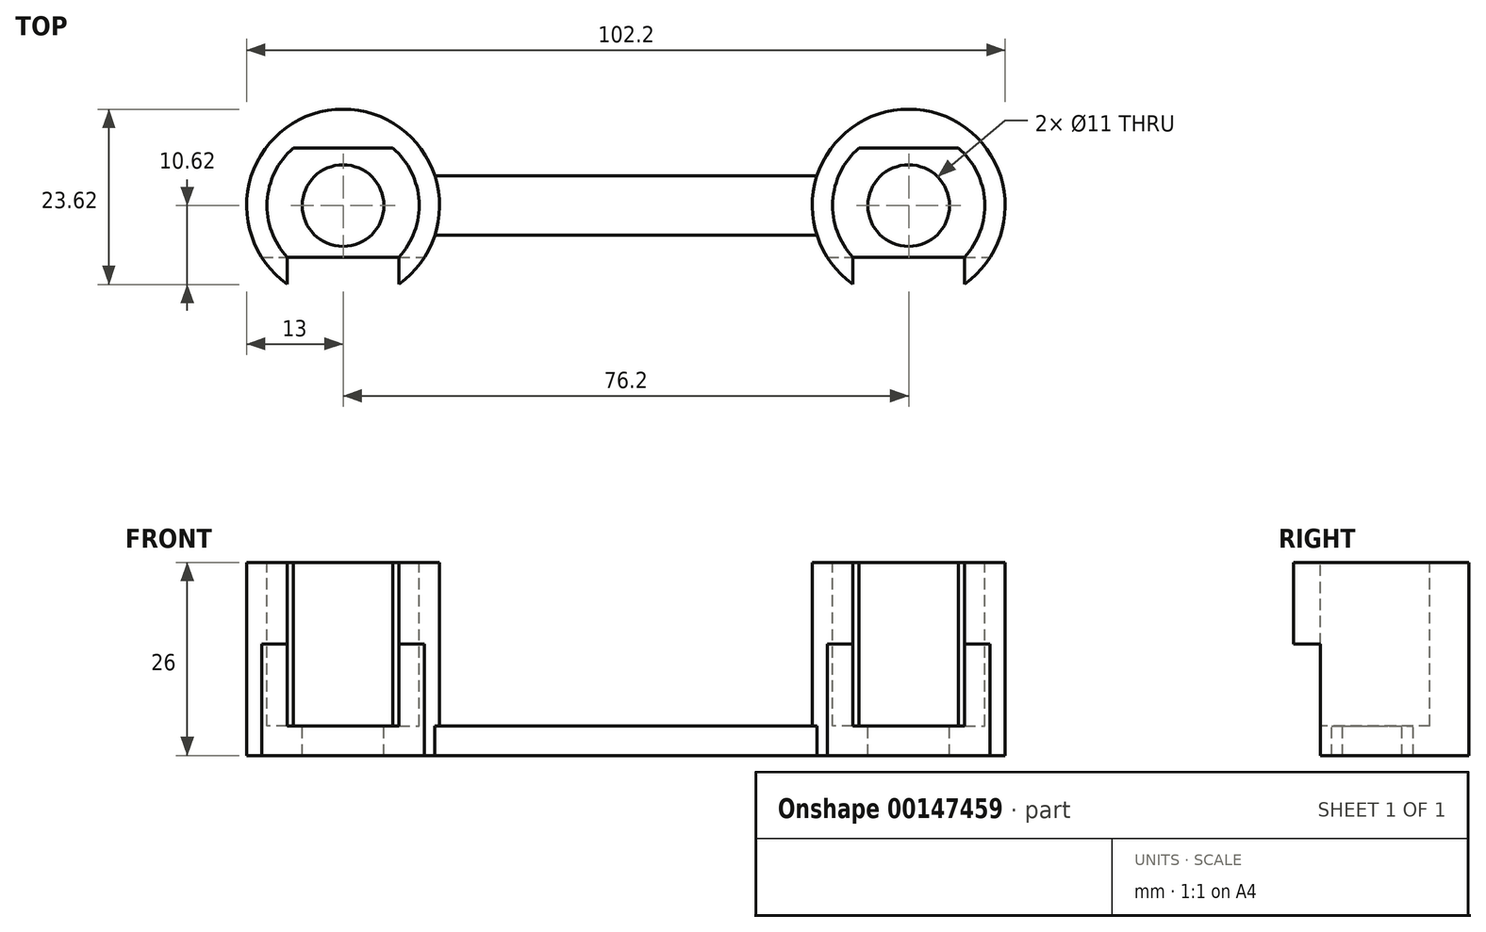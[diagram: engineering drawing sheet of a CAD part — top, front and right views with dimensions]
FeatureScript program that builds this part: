
annotation { "Feature Type Name" : "Feature", "Feature Type Description" : "" }
export const myFeature = defineFeature(function(context is Context, id is Id, definition is map)
    precondition{}
    {
        {
            var Q0;
            Q0=qCreatedBy(makeId("Top.planeOp"),FACE);
            var sketch = newSketch(context, id + "F0", { "sketchPlane" : qUnion([Q0])});
            skPoint(sketch, "E0.middle", {"position": v(-38.1, 0) * mm});
            skPoint(sketch, "E1.orphan", {"position": v(-46.9, 8.41) * mm});
            skPoint(sketch, "E0.left.end.orphan", {"position": v(-49.35, -8.41) * mm});
            skPoint(sketch, "E2.orphan", {"position": v(-29.3, -8.41) * mm});
            skPoint(sketch, "E3.orphan", {"position": v(-26.85, 8.41) * mm});
            skCircle(sketch, "E4", {"center": v(-38.1, 0) * mm, "radius": 13 * mm});
            skPoint(sketch, "E5.middle", {"position": v(38.1, 0) * mm});
            skPoint(sketch, "E6.orphan", {"position": v(29.32, 8.41) * mm});
            skPoint(sketch, "E5.left.end.orphan", {"position": v(26.83, -8.41) * mm});
            skPoint(sketch, "E7.orphan", {"position": v(46.88, -8.41) * mm});
            skPoint(sketch, "E8.orphan", {"position": v(49.37, 8.41) * mm});
            skCircle(sketch, "E9", {"center": v(38.1, 0) * mm, "radius": 13 * mm});
            skLineSegment(sketch, "E10", {"start": v(-38.1, 0) * mm, "end": v(38.1, 0) * mm});
            skSolve(sketch);
        }
        {
            var Q0;
            Q0=qCreatedBy(makeId("Top.planeOp"),FACE);
            var sketch = newSketch(context, id + "F1", { "sketchPlane" : qUnion([Q0])});
            skLineSegment(sketch, "E11", {"start": v(38.1, 0) * mm, "end": v(-38.1, 0) * mm});
            skCircle(sketch, "E12", {"center": v(-38.1, 0) * mm, "radius": 10.25 * mm});
            skCircle(sketch, "E13", {"center": v(38.1, 0) * mm, "radius": 10.25 * mm});
            skLineSegment(sketch, "E14.bottom", {"start": v(-44.8, 7.76) * mm, "end": v(-31.4, 7.76) * mm});
            skLineSegment(sketch, "E14.top", {"start": v(-44.8, -7.76) * mm, "end": v(-31.4, -7.76) * mm});
            skLineSegment(sketch, "E14.left", {"start": v(-44.8, 7.76) * mm, "end": v(-44.8, -7.76) * mm});
            skLineSegment(sketch, "E14.right", {"start": v(-31.4, 7.76) * mm, "end": v(-31.4, -7.76) * mm});
            skLineSegment(sketch, "E15.bottom", {"start": v(44.8, 7.76) * mm, "end": v(31.4, 7.76) * mm});
            skLineSegment(sketch, "E15.top", {"start": v(44.8, -7.76) * mm, "end": v(31.4, -7.76) * mm});
            skLineSegment(sketch, "E15.left", {"start": v(44.8, 7.76) * mm, "end": v(44.8, -7.76) * mm});
            skLineSegment(sketch, "E15.right", {"start": v(31.4, 7.76) * mm, "end": v(31.4, -7.76) * mm});
            skSolve(sketch);
        }
        {
            var Q0;
            Q0 = qSketchRegion(id + "F0", true);
            extrude(context, id + "F2", {"entities" : qUnion([Q0]), "oppositeDirection" : true, "depth" : 26 * mm});
        }
        {
            var Q0;
            {var subQ0=sQuery(id+"F1.wireOp",EDGE,"E12");var subQ1=sQuery(id+"F1.wireOp",EDGE,"E11");var subQ2=makeQuery(id+"F1.imprint","INTERSECT",VERTEX,{"derivedFrom":[subQ1,subQ0]});Q0=makeQuery(id+"F1.imprint","IMPRINT",FACE,{"disambiguationData":[TD([[makeQuery(id+"F1.imprint","IMPRINT",EDGE,{"disambiguationData":[TD([[subQ2,-1.0]])],"derivedFrom":subQ1}),1.0]])]});}
            var Q1;
            {var subQ0=sQuery(id+"F1.wireOp",EDGE,"E12");var subQ1=sQuery(id+"F1.wireOp",EDGE,"E11");var subQ2=makeQuery(id+"F1.imprint","INTERSECT",VERTEX,{"derivedFrom":[subQ1,subQ0]});Q1=makeQuery(id+"F1.imprint","IMPRINT",FACE,{"disambiguationData":[TD([[makeQuery(id+"F1.imprint","IMPRINT",EDGE,{"disambiguationData":[TD([[subQ2,-1.0]])],"derivedFrom":subQ1}),-1.0]])]});}
            var Q2;
            {var subQ1=sQuery(id+"F1.wireOp",EDGE,"E14.bottom");Q2=makeQuery(id+"F1.imprint","IMPRINT",FACE,{"disambiguationData":[TD([[makeQuery(id+"F1.imprint","IMPRINT",EDGE,{"derivedFrom":subQ1}),-1.0]])]});}
            var Q3;
            {var subQ0=sQuery(id+"F1.wireOp",EDGE,"E14.left");Q3=makeQuery(id+"F1.imprint","IMPRINT",FACE,{"disambiguationData":[TD([[makeQuery(id+"F1.imprint","IMPRINT",EDGE,{"derivedFrom":subQ0}),-1.0]])]});}
            var Q4;
            {var subQ1=sQuery(id+"F1.wireOp",EDGE,"E15.bottom");Q4=makeQuery(id+"F1.imprint","IMPRINT",FACE,{"disambiguationData":[TD([[makeQuery(id+"F1.imprint","IMPRINT",EDGE,{"derivedFrom":subQ1}),1.0]])]});}
            var Q5;
            {var subQ0=sQuery(id+"F1.wireOp",EDGE,"E15.left");Q5=makeQuery(id+"F1.imprint","IMPRINT",FACE,{"disambiguationData":[TD([[makeQuery(id+"F1.imprint","IMPRINT",EDGE,{"derivedFrom":subQ0}),1.0]])]});}
            var Q6;
            {var subQ0=sQuery(id+"F1.wireOp",EDGE,"E13");var subQ1=sQuery(id+"F1.wireOp",EDGE,"E11");var subQ2=makeQuery(id+"F1.imprint","INTERSECT",VERTEX,{"derivedFrom":[subQ1,subQ0]});Q6=makeQuery(id+"F1.imprint","IMPRINT",FACE,{"disambiguationData":[TD([[makeQuery(id+"F1.imprint","IMPRINT",EDGE,{"disambiguationData":[TD([[subQ2,1.0]])],"derivedFrom":subQ1}),1.0]])]});}
            var Q7;
            {var subQ0=sQuery(id+"F1.wireOp",EDGE,"E13");var subQ1=sQuery(id+"F1.wireOp",EDGE,"E11");var subQ2=makeQuery(id+"F1.imprint","INTERSECT",VERTEX,{"derivedFrom":[subQ1,subQ0]});Q7=makeQuery(id+"F1.imprint","IMPRINT",FACE,{"disambiguationData":[TD([[makeQuery(id+"F1.imprint","IMPRINT",EDGE,{"disambiguationData":[TD([[subQ2,1.0]])],"derivedFrom":subQ1}),-1.0]])]});}
            extrude(context, id + "F3", {"entities" : qUnion([Q0, Q1, Q2, Q3, Q4, Q5, Q6, Q7]), "operationType" : NewBodyOperationType.REMOVE, "oppositeDirection" : true, "depth" : 22 * mm});
        }
        {
            var Q0;
            Q0=qCreatedBy(makeId("Top.planeOp"),FACE);
            var sketch = newSketch(context, id + "F4", { "sketchPlane" : qUnion([Q0])});
            skLineSegment(sketch, "E16", {"start": v(38.1, 0) * mm, "end": v(-38.1, 0) * mm});
            skCircle(sketch, "E17", {"center": v(-38.1, 0) * mm, "radius": 5.5 * mm});
            skCircle(sketch, "E18", {"center": v(38.1, 0) * mm, "radius": 5.5 * mm});
            skLineSegment(sketch, "E19", {"start": v(-38.1, 0) * mm, "end": v(-38.1, -10) * mm});
            skLineSegment(sketch, "E20.bottom", {"start": v(-45.6, -13) * mm, "end": v(-30.6, -13) * mm});
            skLineSegment(sketch, "E20.top", {"start": v(-45.6, -6.99) * mm, "end": v(-30.6, -6.99) * mm});
            skLineSegment(sketch, "E20.left", {"start": v(-45.6, -13) * mm, "end": v(-45.6, -6.99) * mm});
            skLineSegment(sketch, "E20.right", {"start": v(-30.6, -13) * mm, "end": v(-30.6, -6.99) * mm});
            skPoint(sketch, "E20.middle", {"position": v(-38.1, -10) * mm});
            skLineSegment(sketch, "E21", {"start": v(38.1, 0) * mm, "end": v(38.1, -10) * mm});
            skLineSegment(sketch, "E22.bottom", {"start": v(30.6, -13) * mm, "end": v(45.6, -13) * mm});
            skLineSegment(sketch, "E22.top", {"start": v(30.6, -6.99) * mm, "end": v(45.6, -6.99) * mm});
            skLineSegment(sketch, "E22.left", {"start": v(30.6, -13) * mm, "end": v(30.6, -6.99) * mm});
            skLineSegment(sketch, "E22.right", {"start": v(45.6, -13) * mm, "end": v(45.6, -6.99) * mm});
            skPoint(sketch, "E22.middle", {"position": v(38.1, -10) * mm});
            skSolve(sketch);
        }
        {
            var Q0;
            Q0 = qSketchRegion(id + "F4", true);
            extrude(context, id + "F5", {"entities" : qUnion([Q0]), "operationType" : NewBodyOperationType.REMOVE, "oppositeDirection" : true, "depth" : 30 * mm});
        }
        {
            var Q0;
            Q0=qCreatedBy(makeId("Top.planeOp"),FACE);
            cPlane(context, id + "F6", {"entities" : qUnion([Q0]), "cplaneType" : CPlaneType.OFFSET, "offset" : 26 * mm, "oppositeDirection" : true, "width" : 150 * mm, "height" : 150 * mm});
        }
        {
            var Q0;
            Q0=qCreatedBy(id+"F6.planeOp",FACE);
            var sketch = newSketch(context, id + "F7", { "sketchPlane" : qUnion([Q0])});
            skLineSegment(sketch, "E23.bottom", {"start": v(-26.5, 4) * mm, "end": v(26.5, 4) * mm});
            skLineSegment(sketch, "E23.top", {"start": v(-26.5, -4) * mm, "end": v(26.5, -4) * mm});
            skLineSegment(sketch, "E23.left", {"start": v(-26.5, 4) * mm, "end": v(-26.5, -4) * mm});
            skLineSegment(sketch, "E23.right", {"start": v(26.5, 4) * mm, "end": v(26.5, -4) * mm});
            skPoint(sketch, "E23.middle", {"position": v(0, 0) * mm});
            skSolve(sketch);
        }
        {
            var Q0;
            Q0 = qSketchRegion(id + "F7", true);
            extrude(context, id + "F8", {"entities" : qUnion([Q0]), "operationType" : NewBodyOperationType.ADD, "depth" : 4 * mm});
        }
        {
            var Q0;
            Q0=qCreatedBy(id+"F6.planeOp",FACE);
            var sketch = newSketch(context, id + "F9", { "sketchPlane" : qUnion([Q0])});
            skLineSegment(sketch, "E24", {"start": v(38.1, 0) * mm, "end": v(-38.1, 0) * mm});
            skLineSegment(sketch, "E25.bottom", {"start": v(-50.6, -6.99) * mm, "end": v(-25.6, -6.99) * mm});
            skLineSegment(sketch, "E25.top", {"start": v(-50.6, -11.99) * mm, "end": v(-25.6, -11.99) * mm});
            skLineSegment(sketch, "E25.left", {"start": v(-50.6, -6.99) * mm, "end": v(-50.6, -11.99) * mm});
            skLineSegment(sketch, "E25.right", {"start": v(-25.6, -6.99) * mm, "end": v(-25.6, -11.99) * mm});
            skPoint(sketch, "E25.middle", {"position": v(-38.1, -9.49) * mm});
            skLineSegment(sketch, "E26.bottom", {"start": v(25.6, -6.99) * mm, "end": v(50.6, -6.99) * mm});
            skLineSegment(sketch, "E26.top", {"start": v(25.6, -11.99) * mm, "end": v(50.6, -11.99) * mm});
            skLineSegment(sketch, "E26.left", {"start": v(25.6, -6.99) * mm, "end": v(25.6, -11.99) * mm});
            skLineSegment(sketch, "E26.right", {"start": v(50.6, -6.99) * mm, "end": v(50.6, -11.99) * mm});
            skPoint(sketch, "E26.middle", {"position": v(38.1, -9.49) * mm});
            skSolve(sketch);
        }
        {
            var Q0;
            Q0 = qSketchRegion(id + "F9", true);
            extrude(context, id + "F10", {"entities" : qUnion([Q0]), "operationType" : NewBodyOperationType.REMOVE, "depth" : 15 * mm});
        }
    });
